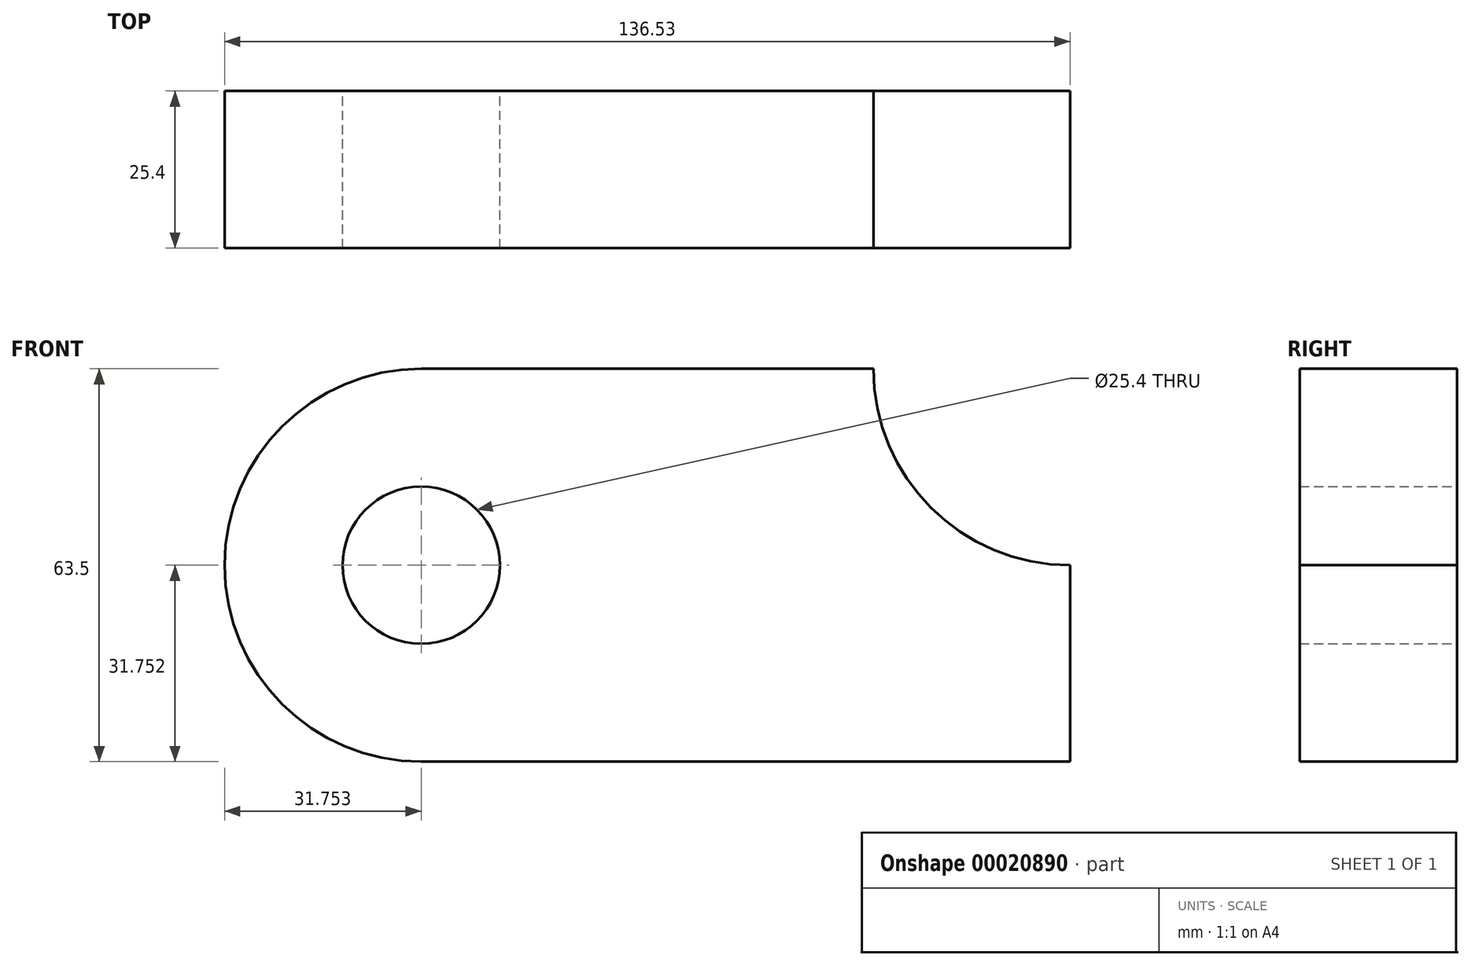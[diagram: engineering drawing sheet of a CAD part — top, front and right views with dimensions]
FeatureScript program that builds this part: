
annotation { "Feature Type Name" : "Feature", "Feature Type Description" : "" }
export const myFeature = defineFeature(function(context is Context, id is Id, definition is map)
    precondition{}
    {
        {
            var Q0;
            Q0=qCreatedBy(makeId("Front.planeOp"),FACE);
            var sketch = newSketch(context, id + "F0", { "sketchPlane" : qUnion([Q0])});
            skLineSegment(sketch, "E0.bottom", {"start": v(-56.86, 39.93) * mm, "end": v(16.17, 39.93) * mm});
            skLineSegment(sketch, "E0.top", {"start": v(-56.86, -23.57) * mm, "end": v(47.92, -23.57) * mm});
            skLineSegment(sketch, "E0.right", {"start": v(47.92, 8.18) * mm, "end": v(47.92, -23.57) * mm});
            skArc(sketch, "E1", {"start": v(-56.86, 39.93) * mm, "mid": v(-88.6, 8.18) * mm, "end": v(-56.86, -23.57) * mm});
            skCircle(sketch, "E2", {"center": v(-56.86, 8.18) * mm, "radius": 12.7 * mm});
            skArc(sketch, "E3", {"start": v(16.17, 39.93) * mm, "mid": v(25.47, 17.48) * mm, "end": v(47.92, 8.18) * mm});
            skSolve(sketch);
        }
        {
            var Q0;
            Q0 = qSketchRegion(id + "F0", true);
            extrude(context, id + "F1", {"entities" : qUnion([Q0]), "depth" : 25.4 * mm});
        }
    });
